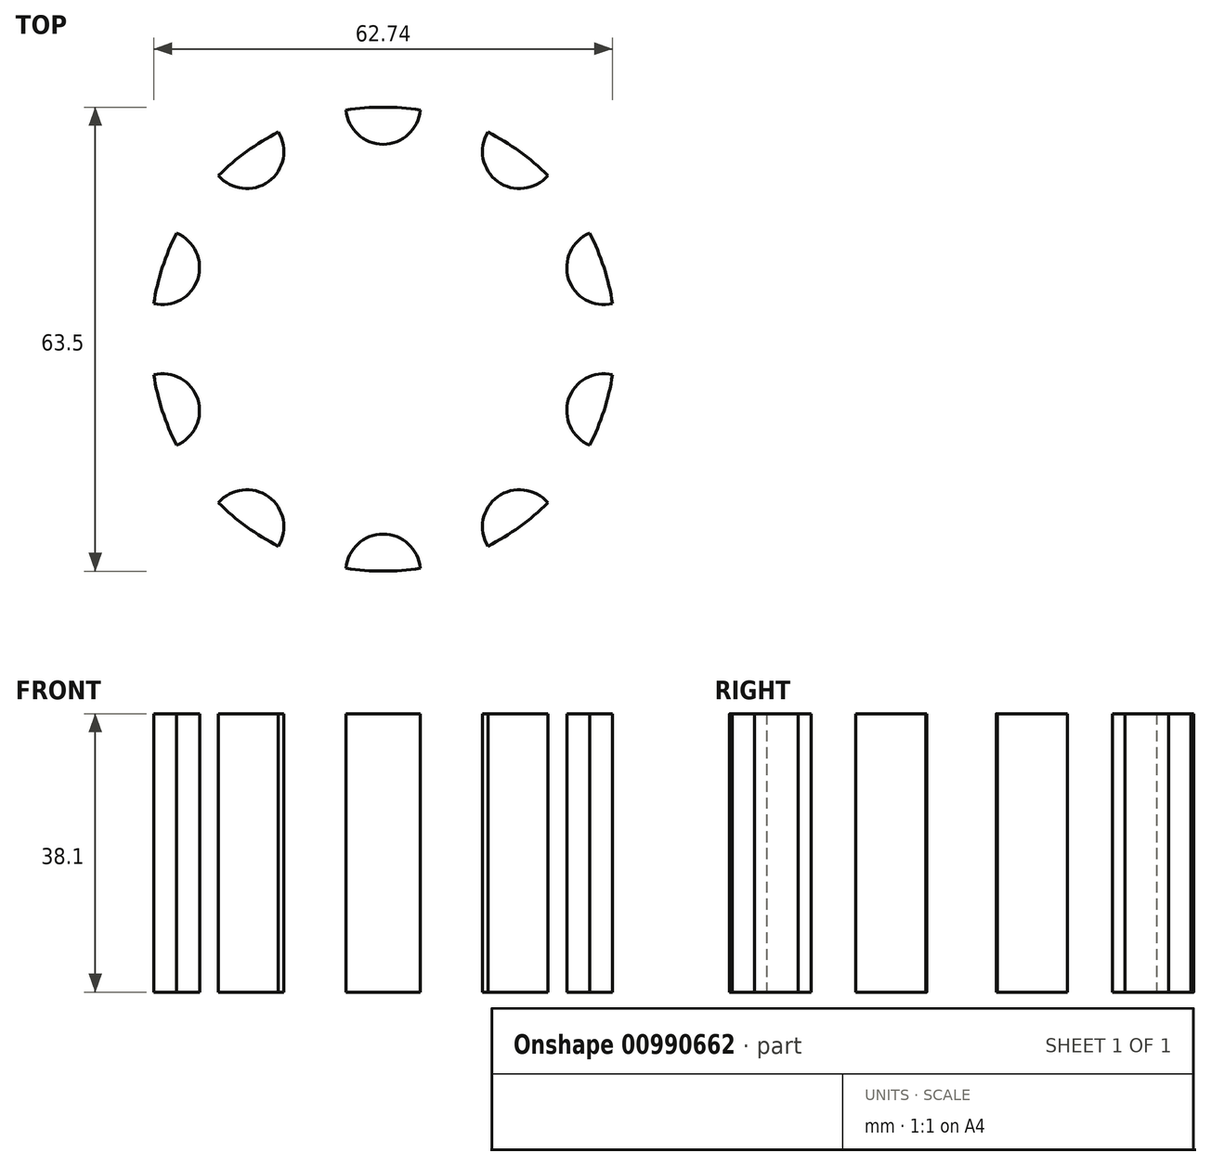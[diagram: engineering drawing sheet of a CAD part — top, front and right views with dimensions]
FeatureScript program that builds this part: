
annotation { "Feature Type Name" : "Feature", "Feature Type Description" : "" }
export const myFeature = defineFeature(function(context is Context, id is Id, definition is map)
    precondition{}
    {
        {
            var Q0;
            Q0=qCreatedBy(makeId("Top.planeOp"),FACE);
            var sketch = newSketch(context, id + "F0", { "sketchPlane" : qUnion([Q0])});
            skCircle(sketch, "E0", {"center": v(0, 0) * mm, "radius": 31.75 * mm});
            skSolve(sketch);
        }
        {
            var Q0;
            Q0=makeQuery(id+"F0.imprint","IMPRINT",FACE,{"disambiguationData":[TD([[makeQuery(id+"F0.imprint","IMPRINT",EDGE,{"derivedFrom":sQuery(id+"F0.wireOp",EDGE,"E0")}),1.0]])]});
            extrude(context, id + "F1", {"entities" : qUnion([Q0]), "depth" : 38.1 * mm});
        }
        {
            var Q0;
            Q0=qCreatedBy(makeId("Top.planeOp"),FACE);
            var sketch = newSketch(context, id + "F2", { "sketchPlane" : qUnion([Q0])});
            skCircle(sketch, "E1", {"center": v(0, 31.75) * mm, "radius": 5.08 * mm});
            skCircle(sketch, "E2.1.0", {"center": v(-18.66, 25.69) * mm, "radius": 5.08 * mm});
            skCircle(sketch, "E2.2.0", {"center": v(-30.2, 9.81) * mm, "radius": 5.08 * mm});
            skCircle(sketch, "E2.3.0", {"center": v(-30.2, -9.81) * mm, "radius": 5.08 * mm});
            skCircle(sketch, "E2.4.0", {"center": v(-18.66, -25.69) * mm, "radius": 5.08 * mm});
            skCircle(sketch, "E2.5.0", {"center": v(0, -31.75) * mm, "radius": 5.08 * mm});
            skCircle(sketch, "E2.6.0", {"center": v(18.66, -25.69) * mm, "radius": 5.08 * mm});
            skCircle(sketch, "E2.7.0", {"center": v(30.2, -9.81) * mm, "radius": 5.08 * mm});
            skCircle(sketch, "E2.8.0", {"center": v(30.2, 9.81) * mm, "radius": 5.08 * mm});
            skCircle(sketch, "E2.9.0", {"center": v(18.66, 25.69) * mm, "radius": 5.08 * mm});
            skPoint(sketch, "E2.center", {"position": v(0, 0) * mm});
            skSolve(sketch);
        }
        {
            var Q0;
            Q0=qSketchRegion(id+"F2",true);
            extrude(context, id + "F3", {"entities" : qUnion([Q0]), "depth" : 50.8 * mm});
        }
        {
            var Q0;
            Q0=makeQuery(id+"F3.opExtrude","SWEPT_BODY",BODY,{"disambiguationData":[OSD([sQuery(id+"F2.wireOp",EDGE,"E2.6.0")])]});
            var Q1;
            Q1=makeQuery(id+"F1.opExtrude","SWEPT_BODY",BODY,{"disambiguationData":[OSD([sQuery(id+"F0.wireOp",EDGE,"E0")])]});
            booleanBodies(context, id + "F4", {"operationType" : BooleanOperationType.INTERSECTION, "tools" : qUnion([Q0, Q1]), "keepTools" : true});
        }
        {
            var Q0;
            Q0=makeQuery(id+"F3.opExtrude","SWEPT_BODY",BODY,{"disambiguationData":[OSD([sQuery(id+"F2.wireOp",EDGE,"E2.7.0")])]});
            var Q1;
            Q1=makeQuery(id+"F1.opExtrude","SWEPT_BODY",BODY,{"disambiguationData":[OSD([sQuery(id+"F0.wireOp",EDGE,"E0")])]});
            booleanBodies(context, id + "F5", {"operationType" : BooleanOperationType.INTERSECTION, "tools" : qUnion([Q0, Q1]), "keepTools" : true});
        }
        {
            var Q0;
            Q0=makeQuery(id+"F3.opExtrude","SWEPT_BODY",BODY,{"disambiguationData":[OSD([sQuery(id+"F2.wireOp",EDGE,"E2.8.0")])]});
            var Q1;
            Q1=makeQuery(id+"F1.opExtrude","SWEPT_BODY",BODY,{"disambiguationData":[OSD([sQuery(id+"F0.wireOp",EDGE,"E0")])]});
            booleanBodies(context, id + "F6", {"operationType" : BooleanOperationType.INTERSECTION, "tools" : qUnion([Q0, Q1]), "keepTools" : true});
        }
        {
            var Q0;
            Q0=makeQuery(id+"F3.opExtrude","SWEPT_BODY",BODY,{"disambiguationData":[OSD([sQuery(id+"F2.wireOp",EDGE,"E2.9.0")])]});
            var Q1;
            Q1=makeQuery(id+"F1.opExtrude","SWEPT_BODY",BODY,{"disambiguationData":[OSD([sQuery(id+"F0.wireOp",EDGE,"E0")])]});
            booleanBodies(context, id + "F7", {"operationType" : BooleanOperationType.INTERSECTION, "tools" : qUnion([Q0, Q1]), "keepTools" : true});
        }
        {
            var Q0;
            Q0=makeQuery(id+"F3.opExtrude","SWEPT_BODY",BODY,{"disambiguationData":[OSD([sQuery(id+"F2.wireOp",EDGE,"E1")])]});
            var Q1;
            Q1=makeQuery(id+"F1.opExtrude","SWEPT_BODY",BODY,{"disambiguationData":[OSD([sQuery(id+"F0.wireOp",EDGE,"E0")])]});
            booleanBodies(context, id + "F8", {"operationType" : BooleanOperationType.INTERSECTION, "tools" : qUnion([Q0, Q1]), "keepTools" : true});
        }
        {
            var Q0;
            Q0=makeQuery(id+"F3.opExtrude","SWEPT_BODY",BODY,{"disambiguationData":[OSD([sQuery(id+"F2.wireOp",EDGE,"E2.1.0")])]});
            var Q1;
            Q1=makeQuery(id+"F1.opExtrude","SWEPT_BODY",BODY,{"disambiguationData":[OSD([sQuery(id+"F0.wireOp",EDGE,"E0")])]});
            booleanBodies(context, id + "F9", {"operationType" : BooleanOperationType.INTERSECTION, "tools" : qUnion([Q0, Q1]), "keepTools" : true});
        }
        {
            var Q0;
            Q0=makeQuery(id+"F3.opExtrude","SWEPT_BODY",BODY,{"disambiguationData":[OSD([sQuery(id+"F2.wireOp",EDGE,"E2.2.0")])]});
            var Q1;
            Q1=makeQuery(id+"F1.opExtrude","SWEPT_BODY",BODY,{"disambiguationData":[OSD([sQuery(id+"F0.wireOp",EDGE,"E0")])]});
            booleanBodies(context, id + "F10", {"operationType" : BooleanOperationType.INTERSECTION, "tools" : qUnion([Q0, Q1]), "keepTools" : true});
        }
        {
            var Q0;
            Q0=makeQuery(id+"F3.opExtrude","SWEPT_BODY",BODY,{"disambiguationData":[OSD([sQuery(id+"F2.wireOp",EDGE,"E2.3.0")])]});
            var Q1;
            Q1=makeQuery(id+"F1.opExtrude","SWEPT_BODY",BODY,{"disambiguationData":[OSD([sQuery(id+"F0.wireOp",EDGE,"E0")])]});
            booleanBodies(context, id + "F11", {"operationType" : BooleanOperationType.INTERSECTION, "tools" : qUnion([Q0, Q1]), "keepTools" : true});
        }
        {
            var Q0;
            Q0=makeQuery(id+"F3.opExtrude","SWEPT_BODY",BODY,{"disambiguationData":[OSD([sQuery(id+"F2.wireOp",EDGE,"E2.4.0")])]});
            var Q1;
            Q1=makeQuery(id+"F1.opExtrude","SWEPT_BODY",BODY,{"disambiguationData":[OSD([sQuery(id+"F0.wireOp",EDGE,"E0")])]});
            booleanBodies(context, id + "F12", {"operationType" : BooleanOperationType.INTERSECTION, "tools" : qUnion([Q0, Q1]), "keepTools" : true});
        }
        {
            var Q0;
            Q0=makeQuery(id+"F3.opExtrude","SWEPT_BODY",BODY,{"disambiguationData":[OSD([sQuery(id+"F2.wireOp",EDGE,"E2.5.0")])]});
            var Q1;
            Q1=makeQuery(id+"F1.opExtrude","SWEPT_BODY",BODY,{"disambiguationData":[OSD([sQuery(id+"F0.wireOp",EDGE,"E0")])]});
            booleanBodies(context, id + "F13", {"operationType" : BooleanOperationType.INTERSECTION, "tools" : qUnion([Q0, Q1]), "keepTools" : true});
        }
        {
            var Q0;
            Q0=makeQuery(id+"F1.opExtrude","SWEPT_BODY",BODY,{"disambiguationData":[OSD([sQuery(id+"F0.wireOp",EDGE,"E0")])]});
            var Q1;
            Q1=makeQuery(id+"F3.opExtrude","SWEPT_BODY",BODY,{"disambiguationData":[OSD([sQuery(id+"F2.wireOp",EDGE,"E1")])]});
            var Q2;
            Q2=makeQuery(id+"F3.opExtrude","SWEPT_BODY",BODY,{"disambiguationData":[OSD([sQuery(id+"F2.wireOp",EDGE,"E2.1.0")])]});
            var Q3;
            Q3=makeQuery(id+"F3.opExtrude","SWEPT_BODY",BODY,{"disambiguationData":[OSD([sQuery(id+"F2.wireOp",EDGE,"E2.2.0")])]});
            var Q4;
            Q4=makeQuery(id+"F3.opExtrude","SWEPT_BODY",BODY,{"disambiguationData":[OSD([sQuery(id+"F2.wireOp",EDGE,"E2.3.0")])]});
            var Q5;
            Q5=makeQuery(id+"F3.opExtrude","SWEPT_BODY",BODY,{"disambiguationData":[OSD([sQuery(id+"F2.wireOp",EDGE,"E2.4.0")])]});
            var Q6;
            Q6=makeQuery(id+"F3.opExtrude","SWEPT_BODY",BODY,{"disambiguationData":[OSD([sQuery(id+"F2.wireOp",EDGE,"E2.5.0")])]});
            var Q7;
            Q7=makeQuery(id+"F3.opExtrude","SWEPT_BODY",BODY,{"disambiguationData":[OSD([sQuery(id+"F2.wireOp",EDGE,"E2.6.0")])]});
            var Q8;
            Q8=makeQuery(id+"F3.opExtrude","SWEPT_BODY",BODY,{"disambiguationData":[OSD([sQuery(id+"F2.wireOp",EDGE,"E2.7.0")])]});
            var Q9;
            Q9=makeQuery(id+"F3.opExtrude","SWEPT_BODY",BODY,{"disambiguationData":[OSD([sQuery(id+"F2.wireOp",EDGE,"E2.8.0")])]});
            var Q10;
            Q10=makeQuery(id+"F3.opExtrude","SWEPT_BODY",BODY,{"disambiguationData":[OSD([sQuery(id+"F2.wireOp",EDGE,"E2.9.0")])]});
            booleanBodies(context, id + "F14", {"operationType" : BooleanOperationType.INTERSECTION, "tools" : qUnion([Q0, Q1, Q2, Q3, Q4, Q5, Q6, Q7, Q8, Q9, Q10])});
        }
    });
